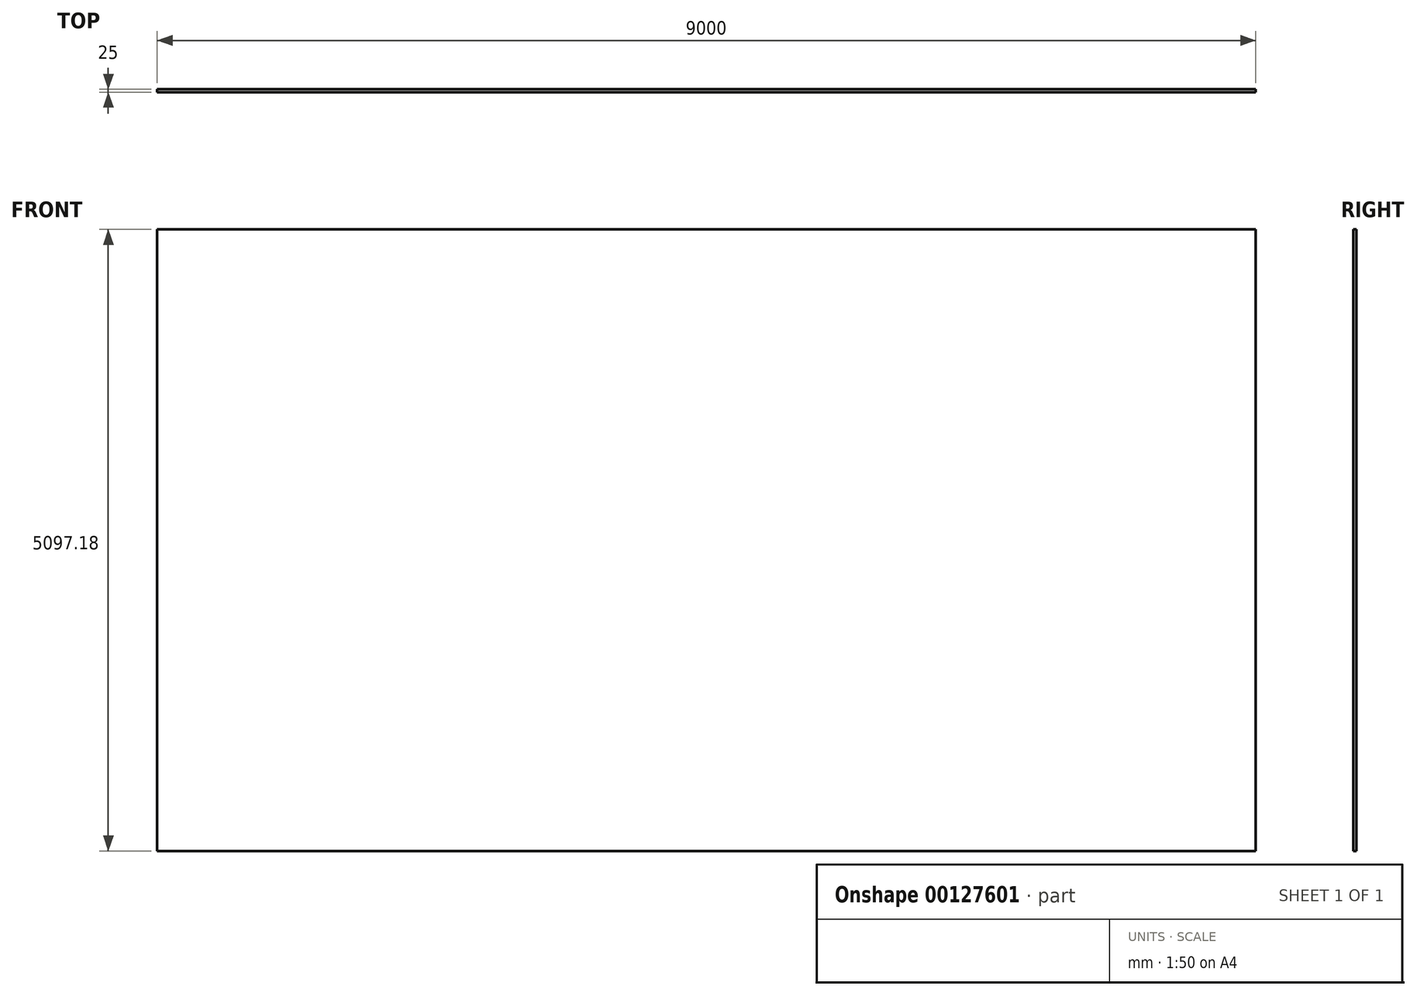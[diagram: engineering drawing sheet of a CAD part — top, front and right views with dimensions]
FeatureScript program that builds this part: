
annotation { "Feature Type Name" : "Feature", "Feature Type Description" : "" }
export const myFeature = defineFeature(function(context is Context, id is Id, definition is map)
    precondition{}
    {
        {
            var Q0;
            Q0=qCreatedBy(makeId("Front.planeOp"),FACE);
            var sketch = newSketch(context, id + "F0", { "sketchPlane" : qUnion([Q0])});
            skLineSegment(sketch, "E0.bottom", {"start": v(-4514.36, 2546.2) * mm, "end": v(4485.64, 2546.2) * mm});
            skLineSegment(sketch, "E0.top", {"start": v(-4514.36, -2550.98) * mm, "end": v(4485.64, -2550.98) * mm});
            skLineSegment(sketch, "E0.left", {"start": v(-4514.36, 2546.2) * mm, "end": v(-4514.36, -2550.98) * mm});
            skLineSegment(sketch, "E0.right", {"start": v(4485.64, 2546.2) * mm, "end": v(4485.64, -2550.98) * mm});
            skSolve(sketch);
        }
        {
            var Q0;
            Q0=makeQuery(id+"F0.imprint","IMPRINT",FACE,{"disambiguationData":[TD([[makeQuery(id+"F0.imprint","IMPRINT",EDGE,{"derivedFrom":sQuery(id+"F0.wireOp",EDGE,"E0.bottom")}),-1.0]])]});
            extrude(context, id + "F1", {"entities" : qUnion([Q0]), "depth" : 25 * mm});
        }
    });
